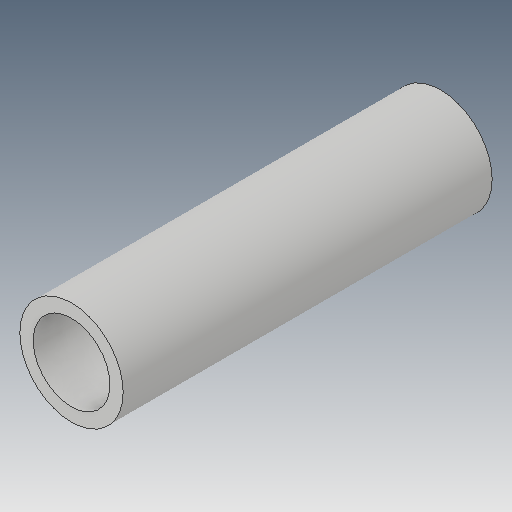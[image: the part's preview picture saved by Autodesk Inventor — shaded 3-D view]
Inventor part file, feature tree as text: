
AUTODESK INVENTOR PART (.ipt)
format: ipt  version: 2017 (Build 210142000, 142)  size: 99,328 bytes
history: native  units: mm
features: other x4, extrude x1, sketch x1, reference x1
ambient origin geometry x8: Origin, YZ Plane, XZ Plane, XY Plane, X Axis, Y Axis, Z Axis, Center Point
bodies: Solid1 (feature_tree)
feature tree (7):
  extrude  "Extrusion1"  Depth=25.0mm
  sketch  "Sketch1"  dims[d0=5.2mm d1=7.0mm d2=25.0mm d3=0.0mm]
  reference  "Reference1"
  parser-record x1  (decoder bookkeeping rows leaked as tree rows — omitted from the tree; the rows remain in map.json)
  other  "Main assembly Test.iam"
  other  "3030bracket_MIR_MIR:2"
  other  "Forged Socket Head Cap Screw - Metric M5x0.8 x 12:1"
note: 1 file-system path scrubbed to <path> (originals preserved in map.json)
